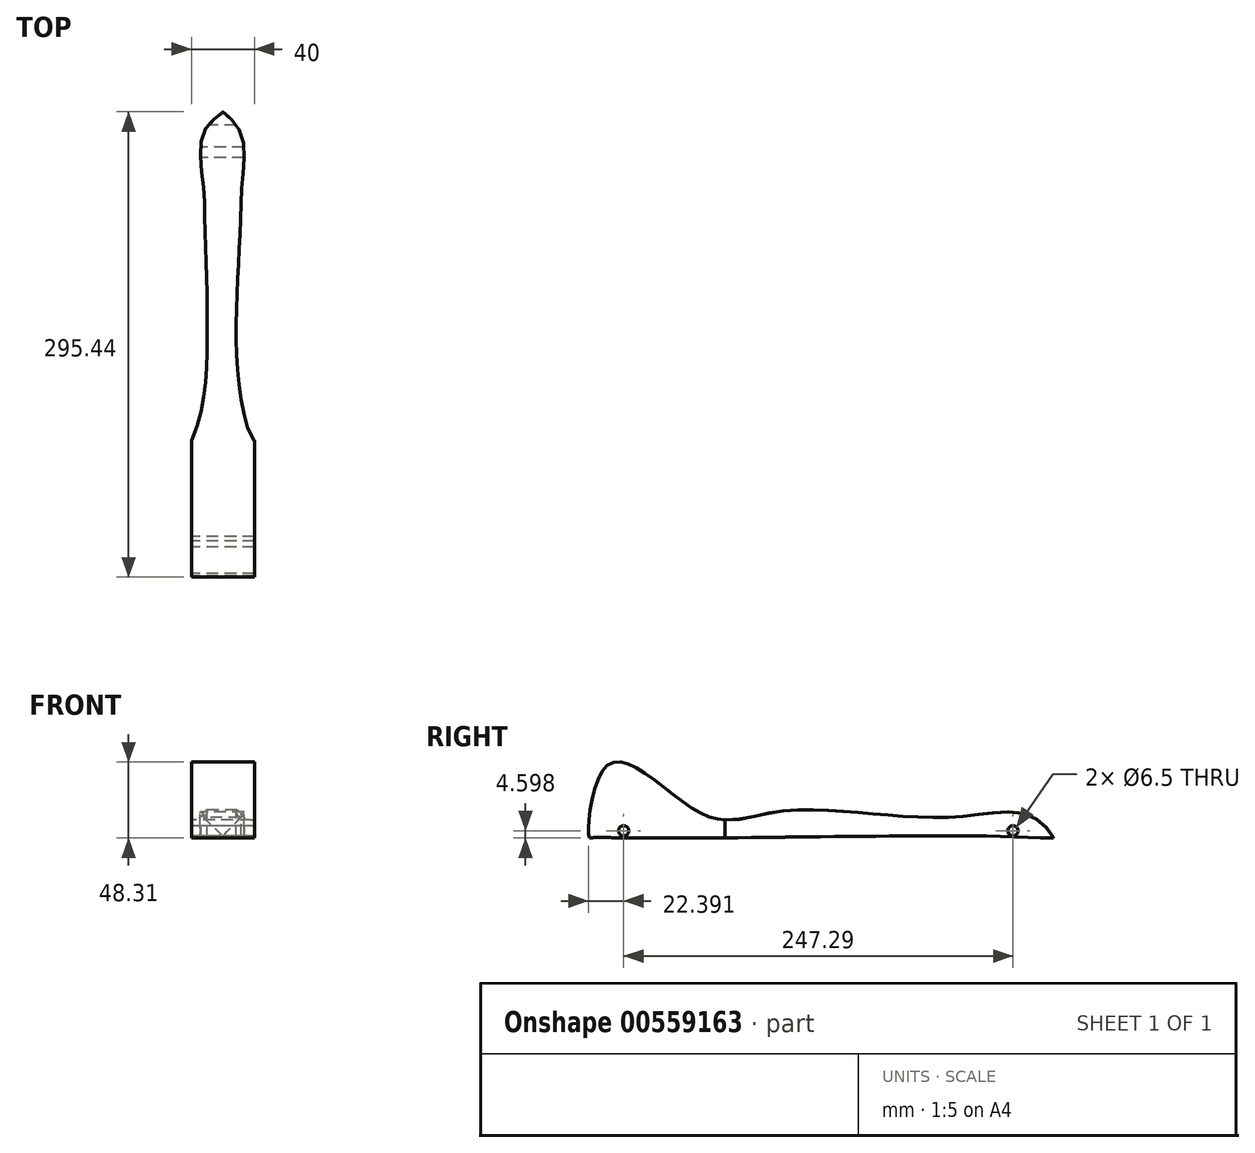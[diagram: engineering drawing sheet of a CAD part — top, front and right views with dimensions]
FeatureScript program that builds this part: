
annotation { "Feature Type Name" : "Feature", "Feature Type Description" : "" }
export const myFeature = defineFeature(function(context is Context, id is Id, definition is map)
    precondition{}
    {
        {
            var Q0;
            Q0=qCreatedBy(makeId("Right.planeOp"),FACE);
            var sketch = newSketch(context, id + "F0", { "sketchPlane" : qUnion([Q0])});
            skLineSegment(sketch, "E0.bottom", {"start": v(-126.96, -35.73) * mm, "end": v(173.04, -35.73) * mm});
            skLineSegment(sketch, "E0.left", {"start": v(-126.96, -35.73) * mm, "end": v(-126.96, 34.27) * mm});
            skLineSegment(sketch, "E0.right", {"start": v(173.04, -35.73) * mm, "end": v(173.04, -15.73) * mm});
            skLineSegment(sketch, "E1", {"start": v(-126.96, 34.27) * mm, "end": v(173.04, -15.73) * mm});
            skCircle(sketch, "E2", {"center": v(147.14, -31.13) * mm, "radius": 3.25 * mm});
            skCircle(sketch, "E3", {"center": v(-100.15, -31.13) * mm, "radius": 3.25 * mm});
            skFitSpline(sketch, "E4", {"points": [v(173.04, -35.73) * mm, v(158.25, -21.75) * mm, v(105.3, -22.58) * mm, v(0, -18.63) * mm, v(-49.21, -20.92) * mm, v(-109.44, 11.07) * mm, v(-121.9, -35.73) * mm, v(-120.24, -35.73) * mm, v(-99.68, -35.73) * mm, v(164.48, -35.73) * mm, v(173.04, -35.73) * mm]});
            skSolve(sketch);
        }
        {
            var Q0;
            Q0=makeQuery(id+"F0.imprint","IMPRINT",FACE,{"disambiguationData":[TD([[makeQuery(id+"F0.imprint","IMPRINT",EDGE,{"derivedFrom":sQuery(id+"F0.wireOp",EDGE,"E0.bottom")}),1.0]])]});
            extrude(context, id + "F1", {"entities" : qUnion([Q0]), "endBound" : BoundingType.SYMMETRIC, "depth" : 40 * mm, "offsetDistance" : 25 * mm});
        }
        {
            var Q0;
            Q0=qCreatedBy(makeId("Top.planeOp"),FACE);
            cPlane(context, id + "F2", {"entities" : qUnion([Q0]), "cplaneType" : CPlaneType.OFFSET, "offset" : 36.4 * mm, "oppositeDirection" : true, "width" : 150 * mm, "height" : 150 * mm});
        }
        {
            var Q0;
            Q0=qCreatedBy(id+"F2.planeOp",FACE);
            var sketch = newSketch(context, id + "F3", { "sketchPlane" : qUnion([Q0])});
            skFitSpline(sketch, "E5", {"points": [v(0, 172.9) * mm, v(12.3, 156.92) * mm, v(11.86, 125.85) * mm, v(11.42, 106.76) * mm, v(10.09, 0) * mm, v(19.4, -36.15) * mm, v(19.85, -35.7) * mm], "startDerivative": vector(108.7, -92.03) * mm, "endDerivative": vector(15.08, 27.89) * mm});
            skFitSpline(sketch, "E6", {"points": [v(0, 172.9) * mm, v(0, 177.75) * mm], "startDerivative": vector(0, 4.86) * mm, "endDerivative": vector(0, 4.86) * mm});
            skFitSpline(sketch, "E7", {"points": [v(0, 176.14) * mm, v(21.7, 176.14) * mm], "startDerivative": vector(21.7, 0) * mm, "endDerivative": vector(21.7, 0) * mm});
            skFitSpline(sketch, "E8", {"points": [v(21.7, 176.14) * mm, v(21.7, 172.9) * mm], "startDerivative": vector(0, -3.24) * mm, "endDerivative": vector(0, -3.24) * mm});
            skFitSpline(sketch, "E9", {"points": [v(19.85, -35.7) * mm, v(24.63, -35.7) * mm], "startDerivative": vector(4.78, 0) * mm, "endDerivative": vector(4.78, 0) * mm});
            skFitSpline(sketch, "E10", {"points": [v(24.63, -35.7) * mm, v(21.7, 172.9) * mm], "startDerivative": vector(-2.94, 208.6) * mm, "endDerivative": vector(-2.94, 208.6) * mm});
            skFitSpline(sketch, "E11", {"points": [v(0, 172.9) * mm, v(-5.23, 168.55) * mm, v(-13.45, 156.92) * mm, v(-12.33, 125.85) * mm, v(-11.58, 106.76) * mm, v(-11.2, 0) * mm, v(-19.8, -35.7) * mm], "startDerivative": vector(-60.58, -49.52) * mm, "endDerivative": vector(-56.47, -146.48) * mm});
            skLineSegment(sketch, "E12", {"start": v(0, 176.14) * mm, "end": v(-13.45, 176.14) * mm});
            skLineSegment(sketch, "E13", {"start": v(-13.45, 176.14) * mm, "end": v(-24.28, 176.14) * mm});
            skLineSegment(sketch, "E14", {"start": v(-19.8, -35.7) * mm, "end": v(-24.28, -35.7) * mm});
            skLineSegment(sketch, "E15", {"start": v(-24.28, -35.7) * mm, "end": v(-24.28, 176.14) * mm});
            skSolve(sketch);
        }
        {
            var Q0;
            Q0=makeQuery(id+"F3.imprint","IMPRINT",FACE,{"disambiguationData":[TD([[makeQuery(id+"F3.imprint","IMPRINT",EDGE,{"derivedFrom":sQuery(id+"F3.wireOp",EDGE,"E5")}),1.0]])]});
            var Q1;
            {var subQ1=sQuery(id+"F3.wireOp",EDGE,"E11");Q1=makeQuery(id+"F3.imprint","IMPRINT",FACE,{"disambiguationData":[TD([[makeQuery(id+"F3.imprint","IMPRINT",EDGE,{"derivedFrom":subQ1}),-1.0]])]});}
            extrude(context, id + "F4", {"entities" : qUnion([Q0, Q1]), "operationType" : NewBodyOperationType.REMOVE, "depth" : 58 * mm, "offsetDistance" : 25 * mm});
        }
    });
